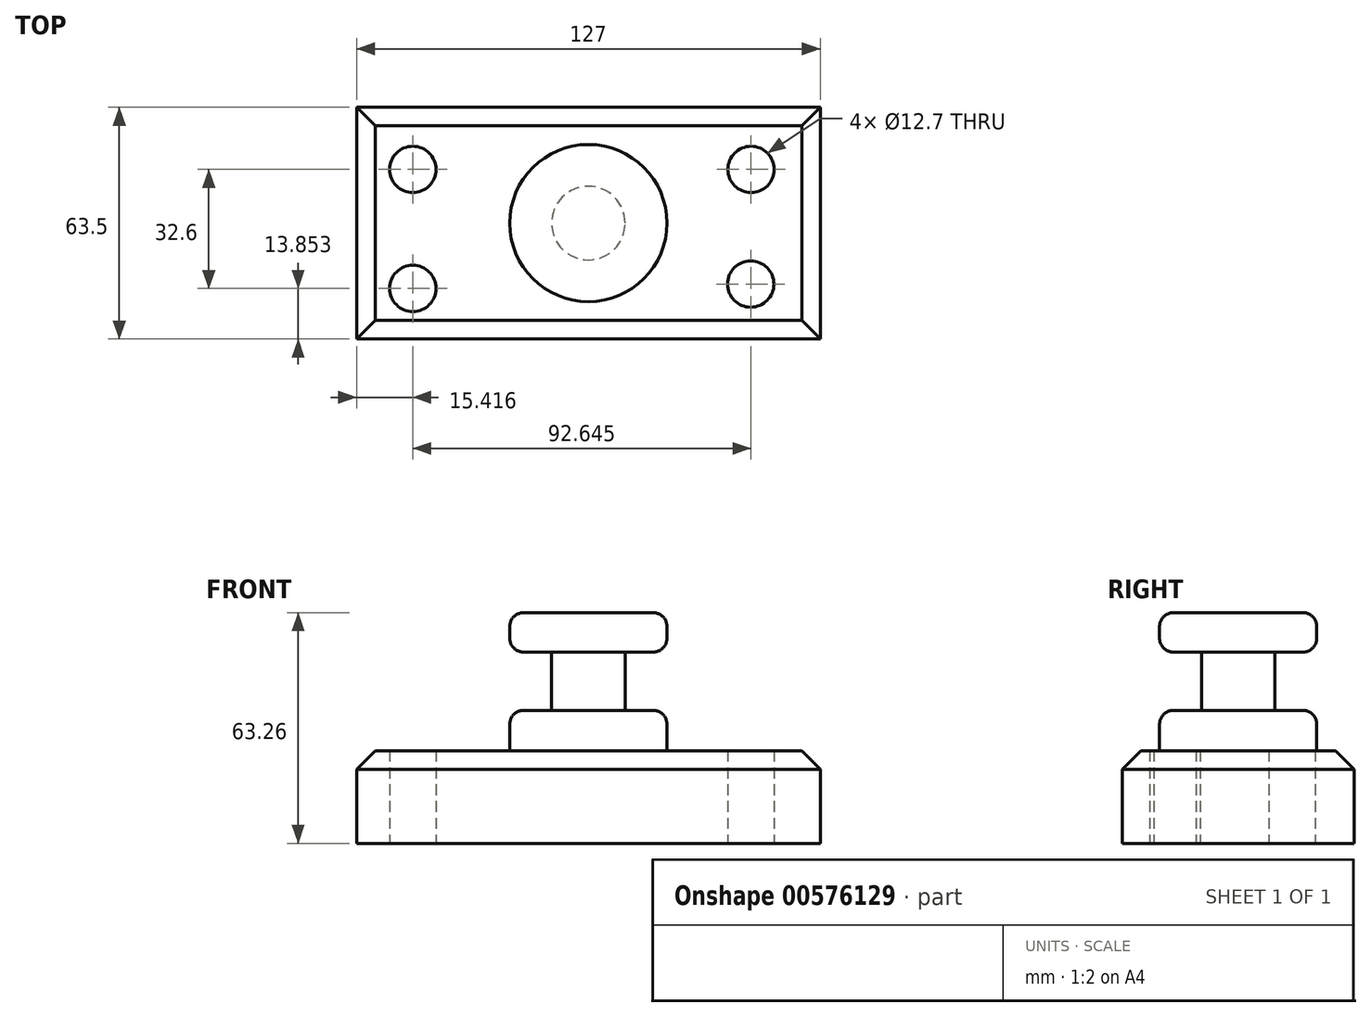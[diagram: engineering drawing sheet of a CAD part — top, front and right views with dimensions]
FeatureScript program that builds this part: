
annotation { "Feature Type Name" : "Feature", "Feature Type Description" : "" }
export const myFeature = defineFeature(function(context is Context, id is Id, definition is map)
    precondition{}
    {
        {
            var Q0;
            Q0=qCreatedBy(makeId("Top.planeOp"),FACE);
            var sketch = newSketch(context, id + "F0", { "sketchPlane" : qUnion([Q0])});
            skLineSegment(sketch, "E0.bottom", {"start": v(63.5, 31.75) * mm, "end": v(-63.5, 31.75) * mm});
            skLineSegment(sketch, "E0.top", {"start": v(63.5, -31.75) * mm, "end": v(-63.5, -31.75) * mm});
            skLineSegment(sketch, "E0.left", {"start": v(63.5, 31.75) * mm, "end": v(63.5, -31.75) * mm});
            skLineSegment(sketch, "E0.right", {"start": v(-63.5, 31.75) * mm, "end": v(-63.5, -31.75) * mm});
            skPoint(sketch, "E0.middle", {"position": v(0, 0) * mm});
            skSolve(sketch);
        }
        {
            var Q0;
            Q0=makeQuery(id+"F0.imprint","IMPRINT",FACE,{"disambiguationData":[TD([[makeQuery(id+"F0.imprint","IMPRINT",EDGE,{"derivedFrom":sQuery(id+"F0.wireOp",EDGE,"E0.bottom")}),1.0]])]});
            extrude(context, id + "F1", {"entities" : qUnion([Q0]), "depth" : 25.4 * mm, "offsetDistance" : 25.4 * mm});
        }
        {
            var Q0;
            Q0=qCreatedBy(makeId("Top.planeOp"),FACE);
            var sketch = newSketch(context, id + "F2", { "sketchPlane" : qUnion([Q0])});
            skCircle(sketch, "E1", {"center": v(-48.08, 14.7) * mm, "radius": 6.14 * mm});
            skCircle(sketch, "E2", {"center": v(-48.08, 14.7) * mm, "radius": 6.35 * mm});
            skCircle(sketch, "E3", {"center": v(-48.08, -17.9) * mm, "radius": 6.35 * mm});
            skCircle(sketch, "E4", {"center": v(44.56, 14.7) * mm, "radius": 6.35 * mm});
            skCircle(sketch, "E5", {"center": v(44.45, -16.7) * mm, "radius": 6.35 * mm});
            skSolve(sketch);
        }
        {
            var Q0;
            Q0=sQuery(id+"F2.wireOp",VERTEX,"E1.center");
            var Q1;
            Q1=sQuery(id+"F2.wireOp",VERTEX,"E3.center");
            var Q2;
            Q2=sQuery(id+"F2.wireOp",VERTEX,"E5.center");
            var Q3;
            Q3=sQuery(id+"F2.wireOp",VERTEX,"E4.center");
            var Q4;
            Q4=makeQuery(id+"F1.opExtrude","SWEPT_BODY",BODY,{"disambiguationData":[OSD([sQuery(id+"F0.wireOp",EDGE,"E0.bottom"),sQuery(id+"F0.wireOp",EDGE,"E0.top"),sQuery(id+"F0.wireOp",EDGE,"E0.left"),sQuery(id+"F0.wireOp",EDGE,"E0.right")])]});
            hole(context, id + "F3", {"style" : HoleStyle.SIMPLE, "endStyle" : HoleEndStyle.THROUGH, "oppositeDirection" : true, "holeDiameter" : 12.7 * mm, "isTappedThrough" : true, "tappedDepth" : 12.7 * mm, "tapClearance" : 3, "locations" : qUnion([Q0, Q1, Q2, Q3]), "scope" : qUnion([Q4])});
        }
        {
            var Q0;
            Q0=qCreatedBy(makeId("Front.planeOp"),FACE);
            var sketch = newSketch(context, id + "F4", { "sketchPlane" : qUnion([Q0])});
            skLineSegment(sketch, "E6.bottom", {"start": v(0, 25.4) * mm, "end": v(-21.53, 25.4) * mm});
            skLineSegment(sketch, "E6.top", {"start": v(0, 63.26) * mm, "end": v(-21.53, 63.26) * mm});
            skLineSegment(sketch, "E6.left", {"start": v(0, 25.4) * mm, "end": v(0, 63.26) * mm});
            skLineSegment(sketch, "E6.right", {"start": v(-21.53, 25.4) * mm, "end": v(-21.53, 63.26) * mm});
            skSolve(sketch);
        }
        {
            var Q0;
            Q0=makeQuery(id+"F4.imprint","IMPRINT",FACE,{"disambiguationData":[TD([[makeQuery(id+"F4.imprint","IMPRINT",EDGE,{"derivedFrom":sQuery(id+"F4.wireOp",EDGE,"E6.bottom")}),-1.0]])]});
            var Q1;
            Q1=sQuery(id+"F4.wireOp",EDGE,"E6.left");
            revolve(context, id + "F5", {"operationType" : NewBodyOperationType.ADD, "entities" : qUnion([Q0]), "axis" : qUnion([Q1]), "revolveType" : RevolveType.FULL});
        }
        {
            var Q0;
            Q0=qCreatedBy(makeId("Front.planeOp"),FACE);
            var sketch = newSketch(context, id + "F6", { "sketchPlane" : qUnion([Q0])});
            skLineSegment(sketch, "E7.bottom", {"start": v(-25.35, 52.45) * mm, "end": v(-10.07, 52.45) * mm});
            skLineSegment(sketch, "E7.top", {"start": v(-25.35, 36.47) * mm, "end": v(-10.07, 36.47) * mm});
            skLineSegment(sketch, "E7.left", {"start": v(-25.35, 52.45) * mm, "end": v(-25.35, 36.47) * mm});
            skLineSegment(sketch, "E7.right", {"start": v(-10.07, 52.45) * mm, "end": v(-10.07, 36.47) * mm});
            skSolve(sketch);
        }
        {
            var Q0;
            Q0=makeQuery(id+"F6.imprint","IMPRINT",FACE,{"disambiguationData":[TD([[makeQuery(id+"F6.imprint","IMPRINT",EDGE,{"derivedFrom":sQuery(id+"F6.wireOp",EDGE,"E7.bottom")}),-1.0]])]});
            var Q1;
            Q1=makeQuery(id+"F5.opRevolve","SWEPT_FACE",FACE,{"disambiguationData":[OSD([sQuery(id+"F4.wireOp",EDGE,"E6.right")])]});
            revolve(context, id + "F7", {"operationType" : NewBodyOperationType.REMOVE, "entities" : qUnion([Q0]), "axis" : qUnion([Q1]), "revolveType" : RevolveType.FULL});
        }
        {
            var Q0;
            Q0=makeQuery(id+"F5.opRevolve","SWEPT_EDGE",EDGE,{"disambiguationData":[OSD([sQuery(id+"F4.wireOp",EDGE,"E6.top"),sQuery(id+"F4.wireOp",EDGE,"E6.right")])]});
            var Q1;
            Q1=makeQuery(id+"F7.boolean.opBoolean","INTERSECT",EDGE,{"derivedFrom":[makeQuery(id+"F5.opRevolve","SWEPT_FACE",FACE,{"disambiguationData":[OSD([sQuery(id+"F4.wireOp",EDGE,"E6.right")])]}),makeQuery(id+"F7.opRevolve","SWEPT_FACE",FACE,{"disambiguationData":[OSD([sQuery(id+"F6.wireOp",EDGE,"E7.top")])]})]});
            var Q2;
            Q2=makeQuery(id+"F5.opRevolve","SWEPT_EDGE",EDGE,{"disambiguationData":[OSD([sQuery(id+"F4.wireOp",EDGE,"E6.bottom"),sQuery(id+"F4.wireOp",EDGE,"E6.right")])]});
            var Q3;
            Q3=makeQuery(id+"F7.boolean.opBoolean","INTERSECT",EDGE,{"derivedFrom":[makeQuery(id+"F5.opRevolve","SWEPT_FACE",FACE,{"disambiguationData":[OSD([sQuery(id+"F4.wireOp",EDGE,"E6.right")])]}),makeQuery(id+"F7.opRevolve","SWEPT_FACE",FACE,{"disambiguationData":[OSD([sQuery(id+"F6.wireOp",EDGE,"E7.bottom")])]})]});
            fillet(context, id + "F8", {"entities" : qUnion([Q0, Q1, Q2, Q3]), "radius" : 3.8 * mm, "tangentPropagation" : true, "allowEdgeOverflow" : false});
        }
        {
            var Q0;
            Q0=makeQuery(id+"F1.opExtrude","CAP_EDGE",EDGE,{"disambiguationData":[OSD([sQuery(id+"F0.wireOp",EDGE,"E0.bottom")])],"isStart":false});
            var Q1;
            Q1=makeQuery(id+"F1.opExtrude","CAP_EDGE",EDGE,{"disambiguationData":[OSD([sQuery(id+"F0.wireOp",EDGE,"E0.right")])],"isStart":false});
            var Q2;
            Q2=makeQuery(id+"F1.opExtrude","CAP_EDGE",EDGE,{"disambiguationData":[OSD([sQuery(id+"F0.wireOp",EDGE,"E0.top")])],"isStart":false});
            var Q3;
            Q3=makeQuery(id+"F1.opExtrude","CAP_EDGE",EDGE,{"disambiguationData":[OSD([sQuery(id+"F0.wireOp",EDGE,"E0.left")])],"isStart":false});
            chamfer(context, id + "F9", {"entities" : qUnion([Q0, Q1, Q2, Q3]), "width" : 5.08 * mm, "tangentPropagation" : true});
        }
    });
